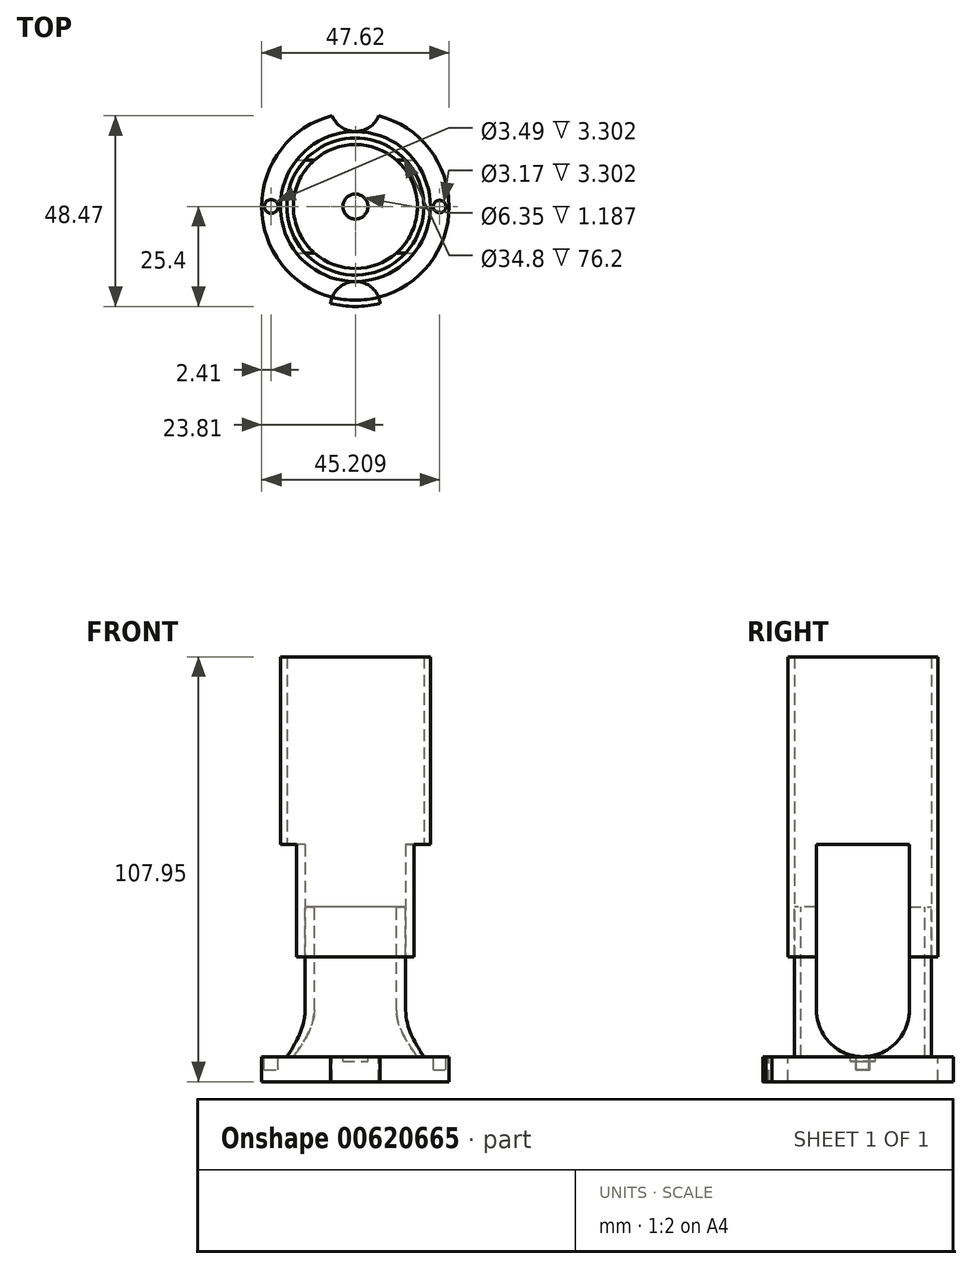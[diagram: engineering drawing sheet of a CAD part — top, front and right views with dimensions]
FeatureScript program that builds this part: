
annotation { "Feature Type Name" : "Feature", "Feature Type Description" : "" }
export const myFeature = defineFeature(function(context is Context, id is Id, definition is map)
    precondition{}
    {
        {
            var Q0;
            Q0=qCreatedBy(makeId("Top.planeOp"),FACE);
            var sketch = newSketch(context, id + "F0", { "sketchPlane" : qUnion([Q0])});
            skCircle(sketch, "E0", {"center": v(0, 0) * mm, "radius": 19.05 * mm});
            skCircle(sketch, "E1", {"center": v(0, 0) * mm, "radius": 17.4 * mm});
            skSolve(sketch);
        }
        {
            var Q0;
            Q0=makeQuery(id+"F0.imprint","IMPRINT",FACE,{"disambiguationData":[TD([[makeQuery(id+"F0.imprint","IMPRINT",EDGE,{"derivedFrom":sQuery(id+"F0.wireOp",EDGE,"E0")}),1.0]])]});
            extrude(context, id + "F1", {"entities" : qUnion([Q0]), "depth" : 76.2 * mm, "offsetDistance" : 25.4 * mm});
        }
        {
            var Q0;
            Q0=qCreatedBy(makeId("Top.planeOp"),FACE);
            var sketch = newSketch(context, id + "F2", { "sketchPlane" : qUnion([Q0])});
            skCircle(sketch, "E2.0", {"center": v(0, 0) * mm, "radius": 17.4 * mm});
            skCircle(sketch, "E3", {"center": v(0, 0) * mm, "radius": 15.75 * mm});
            skSolve(sketch);
        }
        {
            var Q0;
            Q0=makeQuery(id+"F2.imprint","IMPRINT",FACE,{"disambiguationData":[TD([[makeQuery(id+"F2.imprint","IMPRINT",EDGE,{"derivedFrom":sQuery(id+"F2.wireOp",EDGE,"E2.0")}),1.0]])]});
            extrude(context, id + "F3", {"entities" : qUnion([Q0]), "oppositeDirection" : true, "depth" : 25.4 * mm, "offsetDistance" : 25.4 * mm, "hasSecondDirection" : true, "secondDirectionOppositeDirection" : false, "secondDirectionDepth" : 12.7 * mm});
        }
        {
            var Q0;
            Q0=makeQuery(id+"F3.opExtrude","CAP_FACE",FACE,{"disambiguationData":[OSD([sQuery(id+"F2.wireOp",EDGE,"E2.0"),sQuery(id+"F2.wireOp",EDGE,"E3")])],"isStart":false});
            var sketch = newSketch(context, id + "F4", { "sketchPlane" : qUnion([Q0])});
            skCircle(sketch, "E4", {"center": v(0, 0) * mm, "radius": 25.4 * mm});
            skCircle(sketch, "E5", {"center": v(0, 0) * mm, "radius": 23.81 * mm});
            skCircle(sketch, "E6", {"center": v(0, -25.4) * mm, "radius": 6.35 * mm});
            skCircle(sketch, "E7", {"center": v(0, 25.4) * mm, "radius": 6.35 * mm});
            skLineSegment(sketch, "E8", {"start": v(0, 0) * mm, "end": v(25.4, 0) * mm, "construction": true});
            skLineSegment(sketch, "E9", {"start": v(0, 0) * mm, "end": v(-25.4, 0) * mm, "construction": true});
            skCircle(sketch, "E10.0", {"center": v(0, 0) * mm, "radius": 17.4 * mm});
            skLineSegment(sketch, "E11", {"start": v(25.4, 0) * mm, "end": v(21.4, 0) * mm, "construction": true});
            skCircle(sketch, "E12", {"center": v(21.4, 0) * mm, "radius": 1.59 * mm});
            skLineSegment(sketch, "E13", {"start": v(-25.4, 0) * mm, "end": v(-17.4, 0) * mm, "construction": true});
            skLineSegment(sketch, "E14", {"start": v(-25.4, 0) * mm, "end": v(-21.4, 0) * mm, "construction": true});
            skCircle(sketch, "E15", {"center": v(-21.4, 0) * mm, "radius": 1.74 * mm});
            skCircle(sketch, "E16", {"center": v(0, 0) * mm, "radius": 3.18 * mm});
            skSolve(sketch);
        }
        {
            var Q0;
            {var subQ0=sQuery(id+"F4.wireOp",EDGE,"E7");var subQ1=sQuery(id+"F4.wireOp",EDGE,"E4");var subQ2=makeQuery(id+"F4.imprint","INTERSECT",VERTEX,{"disambiguationData":[OD(0.0)],"derivedFrom":[subQ1,subQ0]});Q0=makeQuery(id+"F4.imprint","IMPRINT",FACE,{"disambiguationData":[TD([[makeQuery(id+"F4.imprint","IMPRINT",EDGE,{"disambiguationData":[TD([[subQ2,-1.0]])],"derivedFrom":subQ1}),1.0]])]});}
            var Q1;
            {var subQ0=sQuery(id+"F4.wireOp",EDGE,"E7");var subQ1=sQuery(id+"F4.wireOp",EDGE,"E4");var subQ2=makeQuery(id+"F4.imprint","INTERSECT",VERTEX,{"disambiguationData":[OD(1.0)],"derivedFrom":[subQ1,subQ0]});Q1=makeQuery(id+"F4.imprint","IMPRINT",FACE,{"disambiguationData":[TD([[makeQuery(id+"F4.imprint","IMPRINT",EDGE,{"disambiguationData":[TD([[subQ2,1.0]])],"derivedFrom":subQ1}),1.0]])]});}
            var Q2;
            Q2=makeQuery(id+"F4.imprint","IMPRINT",FACE,{"disambiguationData":[TD([[makeQuery(id+"F4.imprint","IMPRINT",EDGE,{"derivedFrom":makeQuery(id+"F3.opExtrude","CAP_EDGE",EDGE,{"disambiguationData":[OSD([sQuery(id+"F2.wireOp",EDGE,"E2.0")])],"isStart":false})}),1.0]])]});
            var Q3;
            Q3=makeQuery(id+"F4.imprint","IMPRINT",FACE,{"disambiguationData":[TD([[makeQuery(id+"F4.imprint","IMPRINT",EDGE,{"derivedFrom":makeQuery(id+"F3.opExtrude","CAP_EDGE",EDGE,{"disambiguationData":[OSD([sQuery(id+"F2.wireOp",EDGE,"E3")])],"isStart":false})}),-1.0]])]});
            var Q4;
            Q4=makeQuery(id+"F4.imprint","IMPRINT",FACE,{"disambiguationData":[TD([[makeQuery(id+"F4.imprint","IMPRINT",EDGE,{"derivedFrom":makeQuery(id+"F3.opExtrude","CAP_EDGE",EDGE,{"disambiguationData":[OSD([sQuery(id+"F2.wireOp",EDGE,"E2.0")])],"isStart":false})}),-1.0]])]});
            var Q5;
            Q5=makeQuery(id+"F4.imprint","IMPRINT",FACE,{"disambiguationData":[TD([[makeQuery(id+"F4.imprint","IMPRINT",EDGE,{"derivedFrom":sQuery(id+"F4.wireOp",EDGE,"E10.0")}),1.0]])]});
            var Q6;
            Q6=makeQuery(id+"F4.imprint","IMPRINT",FACE,{"disambiguationData":[TD([[makeQuery(id+"F4.imprint","IMPRINT",EDGE,{"derivedFrom":sQuery(id+"F4.wireOp",EDGE,"E15")}),1.0]])]});
            var Q7;
            Q7=makeQuery(id+"F4.imprint","IMPRINT",FACE,{"disambiguationData":[TD([[makeQuery(id+"F4.imprint","IMPRINT",EDGE,{"derivedFrom":sQuery(id+"F4.wireOp",EDGE,"E12")}),1.0]])]});
            var Q8;
            Q8=makeQuery(id+"F4.imprint","IMPRINT",FACE,{"disambiguationData":[TD([[makeQuery(id+"F4.imprint","IMPRINT",EDGE,{"derivedFrom":sQuery(id+"F4.wireOp",EDGE,"E10.0")}),-1.0]])]});
            var Q9;
            Q9=makeQuery(id+"F4.imprint","IMPRINT",FACE,{"disambiguationData":[TD([[makeQuery(id+"F4.imprint","IMPRINT",EDGE,{"derivedFrom":sQuery(id+"F4.wireOp",EDGE,"E16")}),1.0]])]});
            extrude(context, id + "F5", {"entities" : qUnion([Q0, Q1, Q2, Q3, Q4, Q5, Q6, Q7, Q8, Q9]), "operationType" : NewBodyOperationType.ADD, "depth" : 6.35 * mm, "offsetDistance" : 25.4 * mm});
        }
        {
            var Q0;
            Q0=qCreatedBy(makeId("Right.planeOp"),FACE);
            var sketch = newSketch(context, id + "F6", { "sketchPlane" : qUnion([Q0])});
            skLineSegment(sketch, "E17.0", {"start": v(23.81, -25.4) * mm, "end": v(-23.81, -25.4) * mm});
            skLineSegment(sketch, "E18", {"start": v(0, 0) * mm, "end": v(0, -13.6) * mm, "construction": true});
            skCircle(sketch, "E19", {"center": v(0, -13.6) * mm, "radius": 11.8 * mm});
            skLineSegment(sketch, "E20", {"start": v(0, 0) * mm, "end": v(0, 28.51) * mm, "construction": true});
            skLineSegment(sketch, "E21", {"start": v(-11.8, -13.6) * mm, "end": v(-11.8, 28.51) * mm});
            skLineSegment(sketch, "E22", {"start": v(11.8, -13.6) * mm, "end": v(11.8, 28.51) * mm});
            skLineSegment(sketch, "E23", {"start": v(-11.8, 28.51) * mm, "end": v(11.8, 28.51) * mm});
            skSolve(sketch);
        }
        {
            var Q0;
            Q0 = qSketchRegion(id + "F6", true);
            extrude(context, id + "F7", {"entities" : qUnion([Q0]), "operationType" : NewBodyOperationType.REMOVE, "endBound" : BoundingType.THROUGH_ALL, "depth" : 25.4 * mm, "offsetDistance" : 25.4 * mm, "hasSecondDirection" : true, "secondDirectionBound" : SecondDirectionBoundingType.THROUGH_ALL, "secondDirectionOppositeDirection" : true, "secondDirectionDepth" : 25.4 * mm});
        }
        {
            var Q0;
            Q0=makeQuery(id+"F4.imprint","IMPRINT",FACE,{"disambiguationData":[TD([[makeQuery(id+"F4.imprint","IMPRINT",EDGE,{"derivedFrom":sQuery(id+"F4.wireOp",EDGE,"E12")}),1.0]])]});
            var Q1;
            Q1=makeQuery(id+"F4.imprint","IMPRINT",FACE,{"disambiguationData":[TD([[makeQuery(id+"F4.imprint","IMPRINT",EDGE,{"derivedFrom":sQuery(id+"F4.wireOp",EDGE,"E15")}),1.0]])]});
            var Q2;
            Q2=sQuery(id+"F4.wireOp",EDGE,"E15");
            var Q3;
            Q3=sQuery(id+"F4.wireOp",EDGE,"E12");
            extrude(context, id + "F8", {"entities" : qUnion([Q0, Q1]), "operationType" : NewBodyOperationType.REMOVE, "surfaceEntities" : qUnion([Q2, Q3]), "depth" : 3.3 * mm, "offsetDistance" : 25.4 * mm});
        }
        {
            var Q0;
            Q0=makeQuery(id+"F4.imprint","IMPRINT",FACE,{"disambiguationData":[TD([[makeQuery(id+"F4.imprint","IMPRINT",EDGE,{"derivedFrom":sQuery(id+"F4.wireOp",EDGE,"E16")}),1.0]])]});
            extrude(context, id + "F9", {"entities" : qUnion([Q0]), "operationType" : NewBodyOperationType.REMOVE, "depth" : 1.19 * mm, "offsetDistance" : 25.4 * mm});
        }
    });
